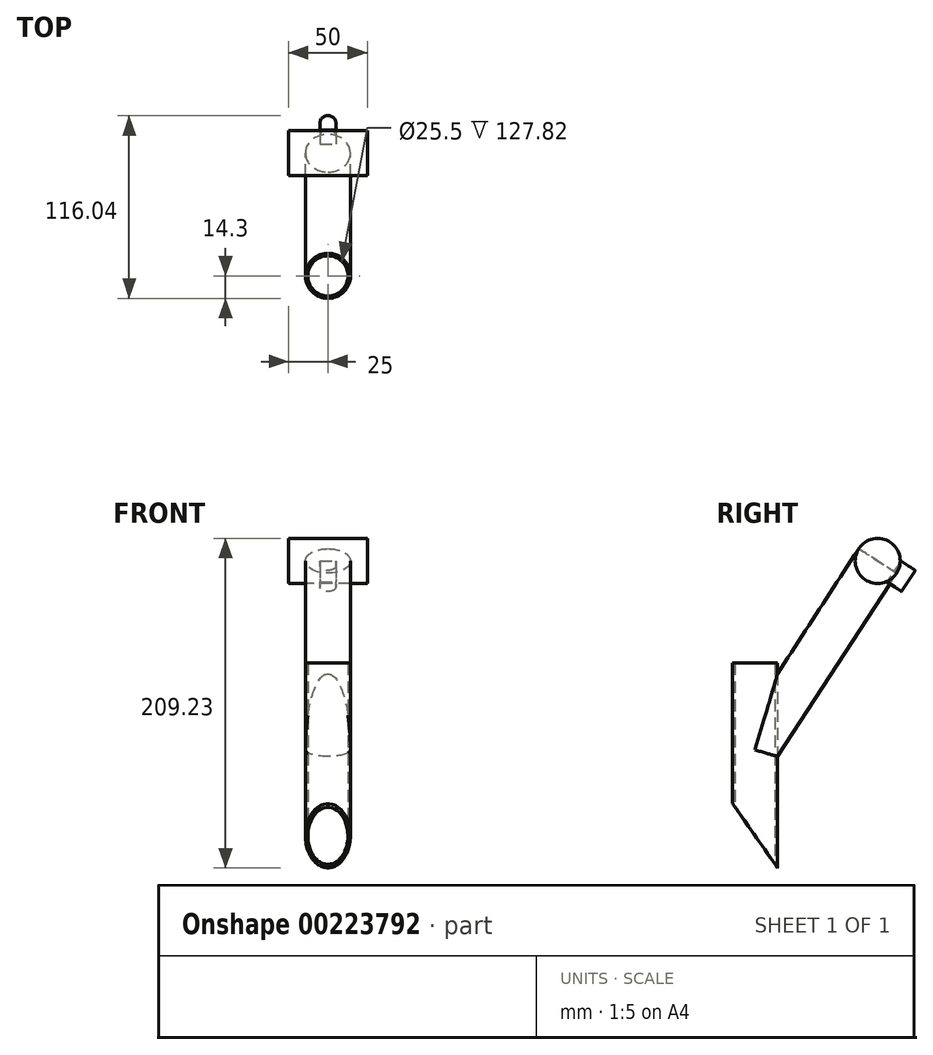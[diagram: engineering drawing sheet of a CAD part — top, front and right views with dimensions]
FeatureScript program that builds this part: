
annotation { "Feature Type Name" : "Feature", "Feature Type Description" : "" }
export const myFeature = defineFeature(function(context is Context, id is Id, definition is map)
    precondition{}
    {
        {
            var Q0;
            Q0=qCreatedBy(makeId("Top.planeOp"),FACE);
            var sketch = newSketch(context, id + "F0", { "sketchPlane" : qUnion([Q0])});
            skCircle(sketch, "E0", {"center": v(0, 0) * mm, "radius": 14.3 * mm});
            skSolve(sketch);
        }
        {
            var Q0;
            Q0=makeQuery(id+"F0.imprint","IMPRINT",FACE,{"disambiguationData":[TD([[makeQuery(id+"F0.imprint","IMPRINT",EDGE,{"derivedFrom":sQuery(id+"F0.wireOp",EDGE,"E0")}),1.0]])]});
            extrude(context, id + "F1", {"entities" : qUnion([Q0]), "depth" : 130 * mm});
        }
        {
            var Q0;
            Q0=makeQuery(id+"F1.opExtrude","CAP_FACE",FACE,{"disambiguationData":[OSD([sQuery(id+"F0.wireOp",EDGE,"E0")])],"isStart":true});
            var sketch = newSketch(context, id + "F2", { "sketchPlane" : qUnion([Q0])});
            skCircle(sketch, "E1", {"center": v(0, 0) * mm, "radius": 12.75 * mm});
            skSolve(sketch);
        }
        {
            var Q0;
            Q0=makeQuery(id+"F2.imprint","IMPRINT",FACE,{"disambiguationData":[TD([[makeQuery(id+"F2.imprint","IMPRINT",EDGE,{"derivedFrom":sQuery(id+"F2.wireOp",EDGE,"E1")}),1.0]])]});
            extrude(context, id + "F3", {"entities" : qUnion([Q0]), "operationType" : NewBodyOperationType.REMOVE, "endBound" : BoundingType.THROUGH_ALL, "oppositeDirection" : true, "depth" : 25 * mm});
        }
        {
            var Q0;
            Q0=qCreatedBy(makeId("Right.planeOp"),FACE);
            var sketch = newSketch(context, id + "F4", { "sketchPlane" : qUnion([Q0])});
            skLineSegment(sketch, "E2", {"start": v(0, 0) * mm, "end": v(0, 75) * mm, "construction": true});
            skLineSegment(sketch, "E3", {"start": v(0, 75) * mm, "end": v(77.88, 194.93) * mm, "construction": true});
            skCircle(sketch, "E4", {"center": v(77.88, 194.93) * mm, "radius": 14.3 * mm});
            skSolve(sketch);
        }
        {
            var Q0;
            Q0=makeQuery(id+"F4.imprint","IMPRINT",FACE,{"disambiguationData":[TD([[makeQuery(id+"F4.imprint","IMPRINT",EDGE,{"derivedFrom":sQuery(id+"F4.wireOp",EDGE,"E4")}),1.0]])]});
            extrude(context, id + "F5", {"entities" : qUnion([Q0]), "depth" : 25 * mm, "hasSecondDirection" : true, "secondDirectionOppositeDirection" : true, "secondDirectionDepth" : 25 * mm});
        }
        {
            var Q0;
            Q0=sQuery(id+"F4.wireOp",VERTEX,"E4.center");
            var Q1;
            Q1=sQuery(id+"F4.wireOp",EDGE,"E3");
            cPlane(context, id + "F6", {"entities" : qUnion([Q0, Q1]), "cplaneType" : CPlaneType.LINE_POINT, "offset" : 25 * mm, "width" : 150 * mm, "height" : 150 * mm});
        }
        {
            var Q0;
            Q0=qCreatedBy(id+"F6.planeOp",FACE);
            var sketch = newSketch(context, id + "F7", { "sketchPlane" : qUnion([Q0])});
            skCircle(sketch, "E5", {"center": v(0, -40.83) * mm, "radius": 14.3 * mm});
            skSolve(sketch);
        }
        {
            var Q0;
            Q0 = qSketchRegion(id + "F7", true);
            var Q1;
            Q1=makeQuery(id+"F1.opExtrude","SWEPT_BODY",BODY,{"disambiguationData":[OSD([sQuery(id+"F0.wireOp",EDGE,"E0")])]});
            extrude(context, id + "F8", {"entities" : qUnion([Q0]), "endBound" : BoundingType.UP_TO_BODY, "oppositeDirection" : true, "endBoundEntityBody" : qUnion([Q1]), "depth" : 143 * mm});
        }
        {
            var Q0;
            Q0=qCreatedBy(makeId("Right.planeOp"),FACE);
            var sketch = newSketch(context, id + "F9", { "sketchPlane" : qUnion([Q0])});
            skLineSegment(sketch, "E6", {"start": v(14.28, 0) * mm, "end": v(-18.54, 46.87) * mm});
            skLineSegment(sketch, "E7", {"start": v(14.28, 0) * mm, "end": v(-18.54, 0) * mm});
            skLineSegment(sketch, "E8", {"start": v(-18.54, 0) * mm, "end": v(-18.54, 46.87) * mm});
            skSolve(sketch);
        }
        {
            var Q0;
            Q0 = qSketchRegion(id + "F9", true);
            extrude(context, id + "F10", {"entities" : qUnion([Q0]), "operationType" : NewBodyOperationType.REMOVE, "oppositeDirection" : true, "depth" : 25 * mm, "hasSecondDirection" : true, "secondDirectionOppositeDirection" : false, "secondDirectionDepth" : 25 * mm});
        }
        {
            var Q0;
            Q0=qCreatedBy(id+"F6.planeOp",FACE);
            var sketch = newSketch(context, id + "F11", { "sketchPlane" : qUnion([Q0])});
            skLineSegment(sketch, "E9.top", {"start": v(-5, -28.6) * mm, "end": v(5, -28.6) * mm});
            skLineSegment(sketch, "E9.left", {"start": v(-5, -22.6) * mm, "end": v(-5, -28.6) * mm});
            skLineSegment(sketch, "E9.right", {"start": v(5, -22.6) * mm, "end": v(5, -28.6) * mm});
            skPoint(sketch, "E9.middle", {"position": v(0, -22.6) * mm});
            skArc(sketch, "E10", {"start": v(-5, -22.6) * mm, "mid": v(0, -17.6) * mm, "end": v(5, -22.6) * mm});
            skPoint(sketch, "E9.bottom.end.orphan", {"position": v(5, -16.6) * mm});
            skPoint(sketch, "E11.orphan", {"position": v(-5, -16.6) * mm});
            skSolve(sketch);
        }
        {
            var Q0;
            Q0 = qSketchRegion(id + "F11", true);
            extrude(context, id + "F12", {"entities" : qUnion([Q0]), "depth" : 8 * mm, "hasSecondDirection" : true, "secondDirectionOppositeDirection" : true, "secondDirectionDepth" : 8 * mm});
        }
    });
